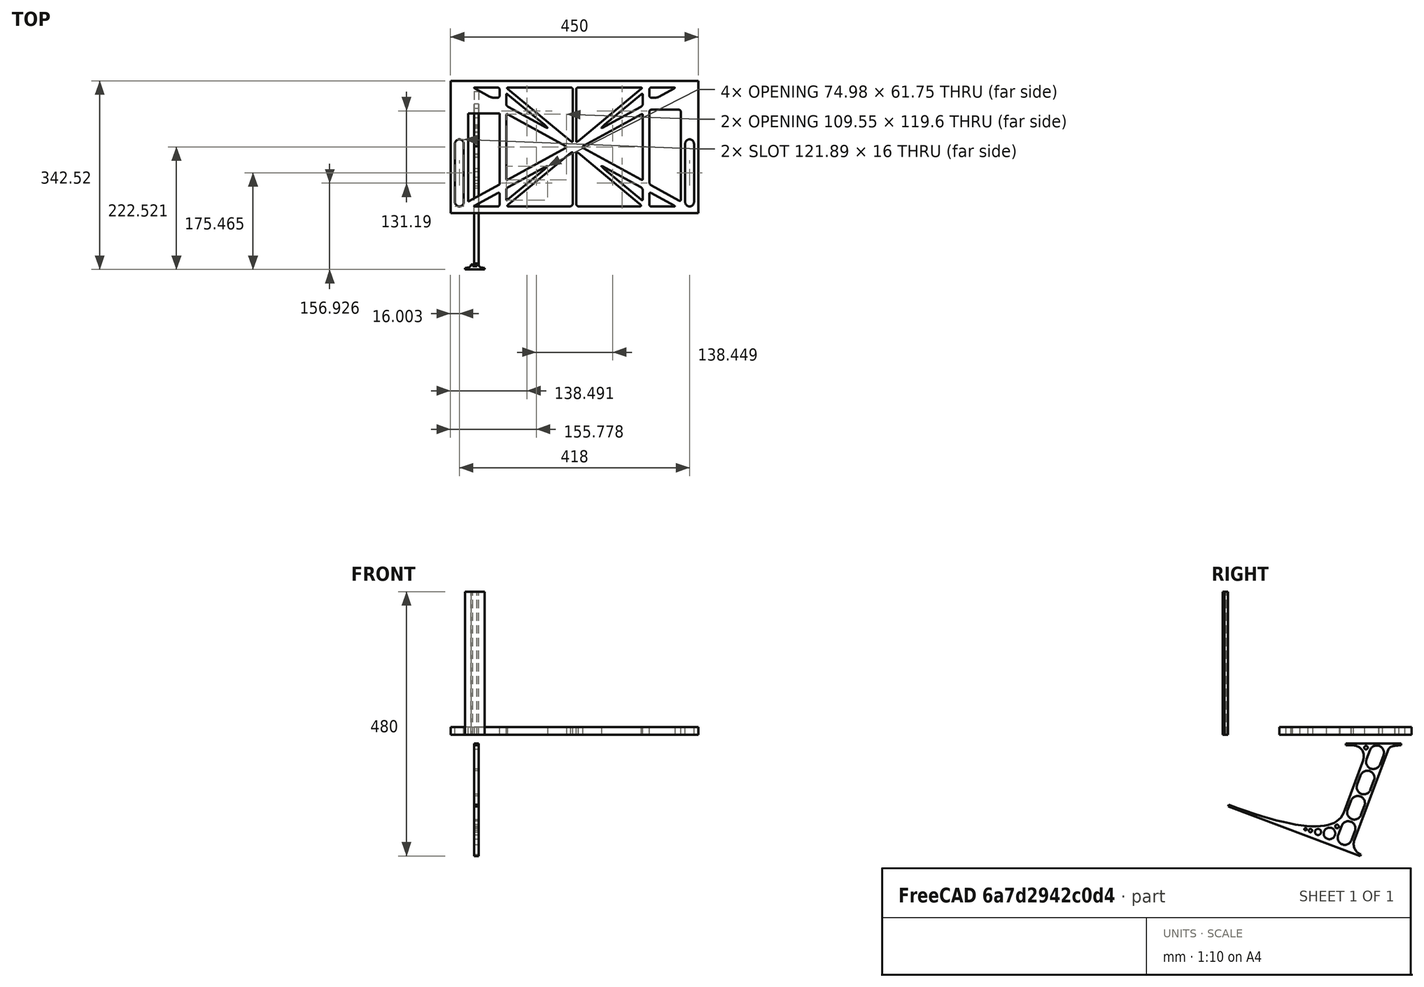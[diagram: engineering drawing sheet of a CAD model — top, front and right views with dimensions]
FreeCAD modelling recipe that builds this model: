
FCSTD DOCUMENT  (FreeCAD 0.19R0.19.2)
Label: laptopStand130FCStd
License: All rights reserved
LicenseURL: http://en.wikipedia.org/wiki/All_rights_reserved
objects: Sketcher::SketchObject×3, Part::Extrusion×3
note: 6 computed .brp shape members not serialized (recipe doc carries the construction recipe); baked Part::Feature solids carry a one-line shape summary decoded from their .brp

FEATURE [Sketcher::SketchObject] Sketch
  FullyConstrained = true
  sketch-geometry (351):
    g0: LineSegment StartX=-10.9272 StartY=-82.7794 StartZ=0 EndX=46.0728 EndY=-51.4823 EndZ=0
    g1: LineSegment StartX=-10.9272 StartY=76.4095 StartZ=0 EndX=-10.9272 EndY=-82.7794 EndZ=0
    g2: LineSegment StartX=46.0728 StartY=76.4095 StartZ=0 EndX=46.0728 EndY=-51.4823 EndZ=0
    g3: LineSegment StartX=-42.9272 StartY=136.221 StartZ=0 EndX=-42.9272 EndY=-103.779 EndZ=0
    g4: LineSegment StartX=407.073 StartY=136.221 StartZ=0 EndX=407.073 EndY=-103.779 EndZ=0
    g5: ArcOfCircle CenterX=-26.9272 CenterY=22.1087 CenterZ=0 NormalX=0 NormalY=0 NormalZ=1 AngleXU=0 Radius=8 StartAngle=1e-16 EndAngle=3.14159
    g6: ArcOfCircle CenterX=-26.9272 CenterY=-83.7794 CenterZ=0 NormalX=0 NormalY=0 NormalZ=1 AngleXU=0 Radius=8 StartAngle=3.14159 EndAngle=6.28319
    g7: LineSegment StartX=-34.9272 StartY=22.1087 StartZ=0 EndX=-34.9272 EndY=-83.7794 EndZ=0
    g8: LineSegment StartX=-18.9272 StartY=22.1087 StartZ=0 EndX=-18.9272 EndY=-83.7794 EndZ=0
    g9: ArcOfCircle CenterX=391.073 CenterY=22.1087 CenterZ=0 NormalX=0 NormalY=0 NormalZ=1 AngleXU=0 Radius=8 StartAngle=-4.4e-15 EndAngle=3.14159
    g10: LineSegment StartX=399.073 StartY=22.1087 StartZ=0 EndX=399.073 EndY=-83.7794 EndZ=0
    g11: LineSegment StartX=383.073 StartY=22.1087 StartZ=0 EndX=383.073 EndY=-83.7794 EndZ=0
    g12: ArcOfCircle CenterX=391.073 CenterY=-83.7794 CenterZ=0 NormalX=0 NormalY=0 NormalZ=1 AngleXU=0 Radius=8 StartAngle=3.14159 EndAngle=6.28319
    g13: Circle CenterX=175.022 CenterY=27.0628 CenterZ=0 NormalX=0 NormalY=0 NormalZ=1 AngleXU=0 Radius=1
    g14: Circle CenterX=179.022 CenterY=24.8665 CenterZ=0 NormalX=0 NormalY=0 NormalZ=1 AngleXU=0 Radius=1
    g15: Circle CenterX=179.022 CenterY=27.0628 CenterZ=0 NormalX=0 NormalY=0 NormalZ=1 AngleXU=0 Radius=1
    g16: BSplineCurve PolesCount=3 KnotsCount=2 Degree=2 IsPeriodic=0
    g17: GeomPoint X=175.022 Y=27.0628 Z=0
    g18: GeomPoint X=179.022 Y=27.0628 Z=0
    g19: Circle CenterX=189.124 CenterY=27.0628 CenterZ=0 NormalX=0 NormalY=0 NormalZ=1 AngleXU=0 Radius=1
    g20: Circle CenterX=185.124 CenterY=24.8665 CenterZ=0 NormalX=0 NormalY=0 NormalZ=1 AngleXU=0 Radius=1
    g21: Circle CenterX=185.124 CenterY=27.0628 CenterZ=0 NormalX=0 NormalY=0 NormalZ=1 AngleXU=0 Radius=1
    g22: BSplineCurve PolesCount=3 KnotsCount=2 Degree=2 IsPeriodic=0
    g23: GeomPoint X=189.124 Y=27.0628 Z=0
    g24: GeomPoint X=185.124 Y=27.0628 Z=0
    g25: Circle CenterX=175.022 CenterY=5.37834 CenterZ=0 NormalX=0 NormalY=0 NormalZ=1 AngleXU=0 Radius=1
    g26: Circle CenterX=179.022 CenterY=7.57463 CenterZ=0 NormalX=0 NormalY=0 NormalZ=1 AngleXU=0 Radius=1
    g27: Circle CenterX=179.022 CenterY=5.34704 CenterZ=0 NormalX=0 NormalY=0 NormalZ=1 AngleXU=0 Radius=1
    g28: BSplineCurve PolesCount=3 KnotsCount=2 Degree=2 IsPeriodic=0
    g29: GeomPoint X=175.022 Y=5.37834 Z=0
    g30: GeomPoint X=179.022 Y=5.34704 Z=0
    g31: Circle CenterX=189.124 CenterY=5.37834 CenterZ=0 NormalX=0 NormalY=0 NormalZ=1 AngleXU=0 Radius=1
    g32: Circle CenterX=185.124 CenterY=7.57463 CenterZ=0 NormalX=0 NormalY=0 NormalZ=1 AngleXU=0 Radius=1
    g33: Circle CenterX=185.124 CenterY=5.34704 CenterZ=0 NormalX=0 NormalY=0 NormalZ=1 AngleXU=0 Radius=1
    g34: BSplineCurve PolesCount=3 KnotsCount=2 Degree=2 IsPeriodic=0
    g35: GeomPoint X=189.124 Y=5.37834 Z=0
    g36: GeomPoint X=185.124 Y=5.34704 Z=0
    g37: Circle CenterX=165.871 CenterY=18.1458 CenterZ=0 NormalX=0 NormalY=0 NormalZ=1 AngleXU=0 Radius=1
    g38: Circle CenterX=169.377 CenterY=16.2206 CenterZ=0 NormalX=0 NormalY=0 NormalZ=1 AngleXU=0 Radius=1
    g39: Circle CenterX=165.871 CenterY=14.2954 CenterZ=0 NormalX=0 NormalY=0 NormalZ=1 AngleXU=0 Radius=1
    g40: BSplineCurve PolesCount=3 KnotsCount=2 Degree=2 IsPeriodic=0
    g41: GeomPoint X=165.871 Y=18.1458 Z=0
    g42: GeomPoint X=165.871 Y=14.2954 Z=0
    g43: Circle CenterX=198.275 CenterY=18.1458 CenterZ=0 NormalX=0 NormalY=0 NormalZ=1 AngleXU=0 Radius=1
    g44: Circle CenterX=194.768 CenterY=16.2206 CenterZ=0 NormalX=0 NormalY=0 NormalZ=1 AngleXU=0 Radius=1
    g45: Circle CenterX=198.275 CenterY=14.2954 CenterZ=0 NormalX=0 NormalY=0 NormalZ=1 AngleXU=0 Radius=1
    g46: BSplineCurve PolesCount=3 KnotsCount=2 Degree=2 IsPeriodic=0
    g47: GeomPoint X=198.275 Y=18.1458 Z=0
    g48: GeomPoint X=198.275 Y=14.2954 Z=0
    g49: LineSegment StartX=407.073 StartY=-103.779 StartZ=0 EndX=-42.9272 EndY=-103.779 EndZ=0
    g50: LineSegment StartX=407.073 StartY=136.221 StartZ=0 EndX=-42.9272 EndY=136.221 EndZ=0
    g51: LineSegment StartX=46.0728 StartY=76.4095 StartZ=0 EndX=-10.9272 EndY=76.4095 EndZ=0
    g52: Circle CenterX=125.607 CenterY=54.1951 CenterZ=0 NormalX=0 NormalY=0 NormalZ=1 AngleXU=0 Radius=1
    g53: Circle CenterX=139.632 CenterY=46.4944 CenterZ=0 NormalX=0 NormalY=0 NormalZ=1 AngleXU=0 Radius=1
    g54: Circle CenterX=127.326 CenterY=56.7187 CenterZ=0 NormalX=0 NormalY=0 NormalZ=1 AngleXU=0 Radius=1
    g55: BSplineCurve PolesCount=3 KnotsCount=2 Degree=2 IsPeriodic=0
    g56: GeomPoint X=125.607 Y=54.1951 Z=0
    g57: GeomPoint X=127.326 Y=56.7187 Z=0
    g58: Circle CenterX=236.821 CenterY=56.7187 CenterZ=0 NormalX=0 NormalY=0 NormalZ=1 AngleXU=0 Radius=1
    g59: Circle CenterX=224.513 CenterY=46.4944 CenterZ=0 NormalX=0 NormalY=0 NormalZ=1 AngleXU=0 Radius=1
    g60: Circle CenterX=238.538 CenterY=54.1951 CenterZ=0 NormalX=0 NormalY=0 NormalZ=1 AngleXU=0 Radius=1
    g61: BSplineCurve PolesCount=3 KnotsCount=2 Degree=2 IsPeriodic=0
    g62: GeomPoint X=236.821 Y=56.7187 Z=0
    g63: GeomPoint X=238.538 Y=54.1951 Z=0
    g64: Circle CenterX=238.538 CenterY=-21.7539 CenterZ=0 NormalX=0 NormalY=0 NormalZ=1 AngleXU=0 Radius=1
    g65: Circle CenterX=224.513 CenterY=-14.0532 CenterZ=0 NormalX=0 NormalY=0 NormalZ=1 AngleXU=0 Radius=1
    g66: Circle CenterX=236.821 CenterY=-24.2775 CenterZ=0 NormalX=0 NormalY=0 NormalZ=1 AngleXU=0 Radius=1
    g67: BSplineCurve PolesCount=3 KnotsCount=2 Degree=2 IsPeriodic=0
    g68: GeomPoint X=238.538 Y=-21.7539 Z=0
    g69: GeomPoint X=236.821 Y=-24.2775 Z=0
    g70: Circle CenterX=125.607 CenterY=-21.7539 CenterZ=0 NormalX=0 NormalY=0 NormalZ=1 AngleXU=0 Radius=1
    g71: Circle CenterX=139.632 CenterY=-14.0532 CenterZ=0 NormalX=0 NormalY=0 NormalZ=1 AngleXU=0 Radius=1
    g72: Circle CenterX=127.325 CenterY=-24.2775 CenterZ=0 NormalX=0 NormalY=0 NormalZ=1 AngleXU=0 Radius=1
    g73: BSplineCurve PolesCount=3 KnotsCount=2 Degree=2 IsPeriodic=0
    g74: GeomPoint X=125.607 Y=-21.7539 Z=0
    g75: GeomPoint X=127.325 Y=-24.2775 Z=0
    g76: Circle CenterX=302.996 CenterY=111.695 CenterZ=0 NormalX=0 NormalY=0 NormalZ=1 AngleXU=0 Radius=1
    g77: Circle CenterX=306.073 CenterY=114.251 CenterZ=0 NormalX=0 NormalY=0 NormalZ=1 AngleXU=0 Radius=1
    g78: Circle CenterX=306.073 CenterY=110.251 CenterZ=0 NormalX=0 NormalY=0 NormalZ=1 AngleXU=0 Radius=1
    g79: BSplineCurve PolesCount=3 KnotsCount=2 Degree=2 IsPeriodic=0
    g80: GeomPoint X=302.996 Y=111.695 Z=0
    g81: GeomPoint X=306.073 Y=110.251 Z=0
    g82: Circle CenterX=306.073 CenterY=95.2763 CenterZ=0 NormalX=0 NormalY=0 NormalZ=1 AngleXU=0 Radius=1
    g83: Circle CenterX=306.073 CenterY=91.2763 CenterZ=0 NormalX=0 NormalY=0 NormalZ=1 AngleXU=0 Radius=1
    g84: Circle CenterX=302.567 CenterY=89.3511 CenterZ=0 NormalX=0 NormalY=0 NormalZ=1 AngleXU=0 Radius=1
    g85: BSplineCurve PolesCount=3 KnotsCount=2 Degree=2 IsPeriodic=0
    g86: GeomPoint X=306.073 Y=95.2763 Z=0
    g87: GeomPoint X=302.567 Y=89.3511 Z=0
    g88: LineSegment StartX=306.073 StartY=110.251 StartZ=0 EndX=306.073 EndY=95.2763 EndZ=0
    g89: LineSegment StartX=302.996 StartY=111.695 StartZ=0 EndX=236.821 EndY=56.7187 EndZ=0
    g90: LineSegment StartX=238.538 StartY=54.1951 StartZ=0 EndX=302.567 EndY=89.3511 EndZ=0
    g91: Circle CenterX=61.1496 CenterY=111.695 CenterZ=0 NormalX=0 NormalY=0 NormalZ=1 AngleXU=0 Radius=1
    g92: Circle CenterX=58.0728 CenterY=114.251 CenterZ=0 NormalX=0 NormalY=0 NormalZ=1 AngleXU=0 Radius=1
    g93: Circle CenterX=58.0728 CenterY=110.251 CenterZ=0 NormalX=0 NormalY=0 NormalZ=1 AngleXU=0 Radius=1
    g94: BSplineCurve PolesCount=3 KnotsCount=2 Degree=2 IsPeriodic=0
    g95: GeomPoint X=61.1496 Y=111.695 Z=0
    g96: GeomPoint X=58.0728 Y=110.251 Z=0
    g97: Circle CenterX=61.5791 CenterY=89.3511 CenterZ=0 NormalX=0 NormalY=0 NormalZ=1 AngleXU=0 Radius=1
    g98: Circle CenterX=58.0728 CenterY=91.2763 CenterZ=0 NormalX=0 NormalY=0 NormalZ=1 AngleXU=0 Radius=1
    g99: Circle CenterX=58.0728 CenterY=95.2763 CenterZ=0 NormalX=0 NormalY=0 NormalZ=1 AngleXU=0 Radius=1
    g100: BSplineCurve PolesCount=3 KnotsCount=2 Degree=2 IsPeriodic=0
    g101: GeomPoint X=61.5791 Y=89.3511 Z=0
    g102: GeomPoint X=58.0728 Y=95.2763 Z=0
    g103: LineSegment StartX=58.0728 StartY=110.251 StartZ=0 EndX=58.0728 EndY=95.2763 EndZ=0
    g104: LineSegment StartX=61.1496 StartY=111.695 StartZ=0 EndX=127.326 EndY=56.7187 EndZ=0
    g105: LineSegment StartX=125.607 StartY=54.1951 StartZ=0 EndX=61.5791 EndY=89.3511 EndZ=0
    g106: Circle CenterX=61.5791 CenterY=-56.9099 CenterZ=0 NormalX=0 NormalY=0 NormalZ=1 AngleXU=0 Radius=1
    g107: Circle CenterX=58.0728 CenterY=-58.8351 CenterZ=0 NormalX=0 NormalY=0 NormalZ=1 AngleXU=0 Radius=1
    g108: Circle CenterX=58.0728 CenterY=-62.8351 CenterZ=0 NormalX=0 NormalY=0 NormalZ=1 AngleXU=0 Radius=1
    g109: BSplineCurve PolesCount=3 KnotsCount=2 Degree=2 IsPeriodic=0
    g110: GeomPoint X=61.5791 Y=-56.9099 Z=0
    g111: GeomPoint X=58.0728 Y=-62.8351 Z=0
    g112: Circle CenterX=58.0728 CenterY=-77.8102 CenterZ=0 NormalX=0 NormalY=0 NormalZ=1 AngleXU=0 Radius=1
    g113: Circle CenterX=58.0728 CenterY=-81.8102 CenterZ=0 NormalX=0 NormalY=0 NormalZ=1 AngleXU=0 Radius=1
    g114: Circle CenterX=61.1496 CenterY=-79.2541 CenterZ=0 NormalX=0 NormalY=0 NormalZ=1 AngleXU=0 Radius=1
    g115: BSplineCurve PolesCount=3 KnotsCount=2 Degree=2 IsPeriodic=0
    g116: GeomPoint X=58.0728 Y=-77.8102 Z=0
    g117: GeomPoint X=61.1496 Y=-79.2541 Z=0
    g118: LineSegment StartX=58.0728 StartY=-62.8351 StartZ=0 EndX=58.0728 EndY=-77.8102 EndZ=0
    g119: LineSegment StartX=61.1496 StartY=-79.2541 StartZ=0 EndX=127.325 EndY=-24.2775 EndZ=0
    g120: LineSegment StartX=125.607 StartY=-21.7539 StartZ=0 EndX=61.5791 EndY=-56.9099 EndZ=0
    g121: Circle CenterX=302.567 CenterY=-56.9099 CenterZ=0 NormalX=0 NormalY=0 NormalZ=1 AngleXU=0 Radius=1
    g122: Circle CenterX=306.073 CenterY=-58.8351 CenterZ=0 NormalX=0 NormalY=0 NormalZ=1 AngleXU=0 Radius=1
    g123: Circle CenterX=306.073 CenterY=-62.8351 CenterZ=0 NormalX=0 NormalY=0 NormalZ=1 AngleXU=0 Radius=1
    g124: BSplineCurve PolesCount=3 KnotsCount=2 Degree=2 IsPeriodic=0
    g125: GeomPoint X=302.567 Y=-56.9099 Z=0
    g126: GeomPoint X=306.073 Y=-62.8351 Z=0
    g127: Circle CenterX=302.996 CenterY=-79.2541 CenterZ=0 NormalX=0 NormalY=0 NormalZ=1 AngleXU=0 Radius=1
    g128: Circle CenterX=306.073 CenterY=-81.8102 CenterZ=0 NormalX=0 NormalY=0 NormalZ=1 AngleXU=0 Radius=1
    g129: Circle CenterX=306.073 CenterY=-77.8102 CenterZ=0 NormalX=0 NormalY=0 NormalZ=1 AngleXU=0 Radius=1
    g130: BSplineCurve PolesCount=3 KnotsCount=2 Degree=2 IsPeriodic=0
    g131: GeomPoint X=302.996 Y=-79.2541 Z=0
    g132: GeomPoint X=306.073 Y=-77.8102 Z=0
    g133: LineSegment StartX=306.073 StartY=-62.8351 StartZ=0 EndX=306.073 EndY=-77.8102 EndZ=0
    g134: LineSegment StartX=302.996 StartY=-79.2541 StartZ=0 EndX=236.821 EndY=-24.2775 EndZ=0
    g135: LineSegment StartX=238.538 StartY=-21.7539 StartZ=0 EndX=302.567 EndY=-56.9099 EndZ=0
    g136: Circle CenterX=61.6457 CenterY=-88.8112 CenterZ=0 NormalX=0 NormalY=0 NormalZ=1 AngleXU=0 Radius=1
    g137: Circle CenterX=58.0728 CenterY=-91.7794 CenterZ=0 NormalX=0 NormalY=0 NormalZ=1 AngleXU=0 Radius=1
    g138: Circle CenterX=63.9135 CenterY=-91.7794 CenterZ=0 NormalX=0 NormalY=0 NormalZ=1 AngleXU=0 Radius=1
    g139: BSplineCurve PolesCount=3 KnotsCount=2 Degree=2 IsPeriodic=0
    g140: GeomPoint X=61.6457 Y=-88.8112 Z=0
    g141: GeomPoint X=63.9135 Y=-91.7794 Z=0
    g142: Circle CenterX=179.022 CenterY=-85.8163 CenterZ=0 NormalX=0 NormalY=0 NormalZ=1 AngleXU=0 Radius=1
    g143: Circle CenterX=179.022 CenterY=-91.7794 CenterZ=0 NormalX=0 NormalY=0 NormalZ=1 AngleXU=0 Radius=1
    g144: Circle CenterX=171.895 CenterY=-91.7794 CenterZ=0 NormalX=0 NormalY=0 NormalZ=1 AngleXU=0 Radius=1
    g145: BSplineCurve PolesCount=3 KnotsCount=2 Degree=2 IsPeriodic=0
    g146: GeomPoint X=179.022 Y=-85.8163 Z=0
    g147: GeomPoint X=171.895 Y=-91.7794 Z=0
    g148: Circle CenterX=185.124 CenterY=-86.2028 CenterZ=0 NormalX=0 NormalY=0 NormalZ=1 AngleXU=0 Radius=1
    g149: Circle CenterX=185.124 CenterY=-91.7794 CenterZ=0 NormalX=0 NormalY=0 NormalZ=1 AngleXU=0 Radius=1
    g150: Circle CenterX=191.747 CenterY=-91.7794 CenterZ=0 NormalX=0 NormalY=0 NormalZ=1 AngleXU=0 Radius=1
    g151: BSplineCurve PolesCount=3 KnotsCount=2 Degree=2 IsPeriodic=0
    g152: GeomPoint X=185.124 Y=-86.2028 Z=0
    g153: GeomPoint X=191.747 Y=-91.7794 Z=0
    g154: Circle CenterX=299.888 CenterY=-86.6413 CenterZ=0 NormalX=0 NormalY=0 NormalZ=1 AngleXU=0 Radius=1
    g155: Circle CenterX=306.073 CenterY=-91.7794 CenterZ=0 NormalX=0 NormalY=0 NormalZ=1 AngleXU=0 Radius=1
    g156: Circle CenterX=298.776 CenterY=-91.7794 CenterZ=0 NormalX=0 NormalY=0 NormalZ=1 AngleXU=0 Radius=1
    g157: BSplineCurve PolesCount=3 KnotsCount=2 Degree=2 IsPeriodic=0
    g158: GeomPoint X=299.888 Y=-86.6413 Z=0
    g159: GeomPoint X=298.776 Y=-91.7794 Z=0
    g160: LineSegment StartX=189.124 StartY=5.37834 StartZ=0 EndX=299.888 EndY=-86.6413 EndZ=0
    g161: LineSegment StartX=298.776 StartY=-91.7794 StartZ=0 EndX=191.747 EndY=-91.7794 EndZ=0
    g162: LineSegment StartX=185.124 StartY=-86.2028 StartZ=0 EndX=185.124 EndY=5.34704 EndZ=0
    g163: LineSegment StartX=179.022 StartY=5.34704 StartZ=0 EndX=179.022 EndY=-85.8163 EndZ=0
    g164: LineSegment StartX=171.895 StartY=-91.7794 StartZ=0 EndX=63.9135 EndY=-91.7794 EndZ=0
    g165: LineSegment StartX=61.6457 StartY=-88.8112 StartZ=0 EndX=175.022 EndY=5.37834 EndZ=0
    g166: Circle CenterX=302.073 CenterY=124.221 CenterZ=0 NormalX=0 NormalY=0 NormalZ=1 AngleXU=0 Radius=1
    g167: Circle CenterX=306.073 CenterY=124.221 CenterZ=0 NormalX=0 NormalY=0 NormalZ=1 AngleXU=0 Radius=1
    g168: Circle CenterX=302.996 CenterY=121.665 CenterZ=0 NormalX=0 NormalY=0 NormalZ=1 AngleXU=0 Radius=1
    g169: BSplineCurve PolesCount=3 KnotsCount=2 Degree=2 IsPeriodic=0
    g170: GeomPoint X=302.073 Y=124.221 Z=0
    g171: GeomPoint X=302.996 Y=121.665 Z=0
    g172: Circle CenterX=189.124 CenterY=124.221 CenterZ=0 NormalX=0 NormalY=0 NormalZ=1 AngleXU=0 Radius=1
    g173: Circle CenterX=185.124 CenterY=124.221 CenterZ=0 NormalX=0 NormalY=0 NormalZ=1 AngleXU=0 Radius=1
    g174: Circle CenterX=185.124 CenterY=120.221 CenterZ=0 NormalX=0 NormalY=0 NormalZ=1 AngleXU=0 Radius=1
    g175: BSplineCurve PolesCount=3 KnotsCount=2 Degree=2 IsPeriodic=0
    g176: GeomPoint X=189.124 Y=124.221 Z=0
    g177: GeomPoint X=185.124 Y=120.221 Z=0
    g178: Circle CenterX=175.022 CenterY=124.221 CenterZ=0 NormalX=0 NormalY=0 NormalZ=1 AngleXU=0 Radius=1
    g179: Circle CenterX=179.022 CenterY=124.221 CenterZ=0 NormalX=0 NormalY=0 NormalZ=1 AngleXU=0 Radius=1
    g180: Circle CenterX=179.022 CenterY=120.221 CenterZ=0 NormalX=0 NormalY=0 NormalZ=1 AngleXU=0 Radius=1
    g181: BSplineCurve PolesCount=3 KnotsCount=2 Degree=2 IsPeriodic=0
    g182: GeomPoint X=175.022 Y=124.221 Z=0
    g183: GeomPoint X=179.022 Y=120.221 Z=0
    g184: Circle CenterX=62.0728 CenterY=124.221 CenterZ=0 NormalX=0 NormalY=0 NormalZ=1 AngleXU=0 Radius=1
    g185: Circle CenterX=58.0728 CenterY=124.221 CenterZ=0 NormalX=0 NormalY=0 NormalZ=1 AngleXU=0 Radius=1
    g186: Circle CenterX=61.1496 CenterY=121.665 CenterZ=0 NormalX=0 NormalY=0 NormalZ=1 AngleXU=0 Radius=1
    g187: BSplineCurve PolesCount=3 KnotsCount=2 Degree=2 IsPeriodic=0
    g188: GeomPoint X=62.0728 Y=124.221 Z=0
    g189: GeomPoint X=61.1496 Y=121.665 Z=0
    g190: LineSegment StartX=62.0728 StartY=124.221 StartZ=0 EndX=175.022 EndY=124.221 EndZ=0
    g191: LineSegment StartX=179.022 StartY=120.221 StartZ=0 EndX=179.022 EndY=27.0628 EndZ=0
    g192: LineSegment StartX=185.124 StartY=27.0628 StartZ=0 EndX=185.124 EndY=120.221 EndZ=0
    g193: LineSegment StartX=189.124 StartY=124.221 StartZ=0 EndX=302.073 EndY=124.221 EndZ=0
    g194: LineSegment StartX=302.996 StartY=121.665 StartZ=0 EndX=189.124 EndY=27.0628 EndZ=0
    g195: LineSegment StartX=175.022 StartY=27.0628 StartZ=0 EndX=61.1496 EndY=121.665 EndZ=0
    g196: Circle CenterX=61.5791 CenterY=75.4095 CenterZ=0 NormalX=0 NormalY=0 NormalZ=1 AngleXU=0 Radius=1
    g197: Circle CenterX=58.0728 CenterY=77.3346 CenterZ=0 NormalX=0 NormalY=0 NormalZ=1 AngleXU=0 Radius=1
    g198: Circle CenterX=58.0728 CenterY=73.3346 CenterZ=0 NormalX=0 NormalY=0 NormalZ=1 AngleXU=0 Radius=1
    g199: BSplineCurve PolesCount=3 KnotsCount=2 Degree=2 IsPeriodic=0
    g200: GeomPoint X=61.5791 Y=75.4095 Z=0
    g201: GeomPoint X=58.0728 Y=73.3346 Z=0
    g202: Circle CenterX=58.0728 CenterY=-40.8935 CenterZ=0 NormalX=0 NormalY=0 NormalZ=1 AngleXU=0 Radius=1
    g203: Circle CenterX=58.0728 CenterY=-44.8935 CenterZ=0 NormalX=0 NormalY=0 NormalZ=1 AngleXU=0 Radius=1
    g204: Circle CenterX=61.5791 CenterY=-42.9683 CenterZ=0 NormalX=0 NormalY=0 NormalZ=1 AngleXU=0 Radius=1
    g205: BSplineCurve PolesCount=3 KnotsCount=2 Degree=2 IsPeriodic=0
    g206: GeomPoint X=58.0728 Y=-40.8935 Z=0
    g207: GeomPoint X=61.5791 Y=-42.9683 Z=0
    g208: LineSegment StartX=61.5791 StartY=-42.9683 StartZ=0 EndX=165.871 EndY=14.2954 EndZ=0
    g209: LineSegment StartX=165.871 StartY=18.1458 StartZ=0 EndX=61.5791 EndY=75.4095 EndZ=0
    g210: LineSegment StartX=58.0728 StartY=73.3346 StartZ=0 EndX=58.0728 EndY=-40.8935 EndZ=0
    g211: Circle CenterX=302.567 CenterY=-42.9683 CenterZ=0 NormalX=0 NormalY=0 NormalZ=1 AngleXU=0 Radius=1
    g212: Circle CenterX=306.073 CenterY=-44.8935 CenterZ=0 NormalX=0 NormalY=0 NormalZ=1 AngleXU=0 Radius=1
    g213: Circle CenterX=306.073 CenterY=-40.8935 CenterZ=0 NormalX=0 NormalY=0 NormalZ=1 AngleXU=0 Radius=1
    g214: BSplineCurve PolesCount=3 KnotsCount=2 Degree=2 IsPeriodic=0
    g215: GeomPoint X=302.567 Y=-42.9683 Z=0
    g216: GeomPoint X=306.073 Y=-40.8935 Z=0
    g217: Circle CenterX=306.073 CenterY=73.3346 CenterZ=0 NormalX=0 NormalY=0 NormalZ=1 AngleXU=0 Radius=1
    g218: Circle CenterX=306.073 CenterY=77.3346 CenterZ=0 NormalX=0 NormalY=0 NormalZ=1 AngleXU=0 Radius=1
    g219: Circle CenterX=302.567 CenterY=75.4095 CenterZ=0 NormalX=0 NormalY=0 NormalZ=1 AngleXU=0 Radius=1
    g220: BSplineCurve PolesCount=3 KnotsCount=2 Degree=2 IsPeriodic=0
    g221: GeomPoint X=306.073 Y=73.3346 Z=0
    g222: GeomPoint X=302.567 Y=75.4095 Z=0
    g223: LineSegment StartX=302.567 StartY=-42.9683 StartZ=0 EndX=198.275 EndY=14.2954 EndZ=0
    g224: LineSegment StartX=198.275 StartY=18.1458 StartZ=0 EndX=302.567 EndY=75.4095 EndZ=0
    g225: LineSegment StartX=306.073 StartY=73.3346 StartZ=0 EndX=306.073 EndY=-40.8935 EndZ=0
    g226: LineSegment StartX=322.073 StartY=105.865 StartZ=0 EndX=328.643 EndY=105.865 EndZ=0
    g227: LineSegment StartX=318.073 StartY=120.221 StartZ=0 EndX=318.073 EndY=109.865 EndZ=0
    g228: LineSegment StartX=336.157 StartY=107.779 StartZ=0 EndX=362.567 EndY=122.294 EndZ=0
    g229: Circle CenterX=362.073 CenterY=124.221 CenterZ=0 NormalX=0 NormalY=0 NormalZ=1 AngleXU=0 Radius=1
    g230: Circle CenterX=366.073 CenterY=124.221 CenterZ=0 NormalX=0 NormalY=0 NormalZ=1 AngleXU=0 Radius=1
    g231: Circle CenterX=362.567 CenterY=122.294 CenterZ=0 NormalX=0 NormalY=0 NormalZ=1 AngleXU=0 Radius=1
    g232: BSplineCurve PolesCount=3 KnotsCount=2 Degree=2 IsPeriodic=0
    g233: GeomPoint X=362.073 Y=124.221 Z=0
    g234: GeomPoint X=362.567 Y=122.294 Z=0
    g235: Circle CenterX=322.073 CenterY=124.221 CenterZ=0 NormalX=0 NormalY=0 NormalZ=1 AngleXU=0 Radius=1
    g236: Circle CenterX=318.073 CenterY=124.221 CenterZ=0 NormalX=0 NormalY=0 NormalZ=1 AngleXU=0 Radius=1
    g237: Circle CenterX=318.073 CenterY=120.221 CenterZ=0 NormalX=0 NormalY=0 NormalZ=1 AngleXU=0 Radius=1
    g238: BSplineCurve PolesCount=3 KnotsCount=2 Degree=2 IsPeriodic=0
    g239: GeomPoint X=322.073 Y=124.221 Z=0
    g240: GeomPoint X=318.073 Y=120.221 Z=0
    g241: Circle CenterX=322.073 CenterY=105.865 CenterZ=0 NormalX=0 NormalY=0 NormalZ=1 AngleXU=0 Radius=1
    g242: Circle CenterX=318.073 CenterY=105.865 CenterZ=0 NormalX=0 NormalY=0 NormalZ=1 AngleXU=0 Radius=1
    g243: Circle CenterX=318.073 CenterY=109.865 CenterZ=0 NormalX=0 NormalY=0 NormalZ=1 AngleXU=0 Radius=1
    g244: BSplineCurve PolesCount=3 KnotsCount=2 Degree=2 IsPeriodic=0
    g245: GeomPoint X=322.073 Y=105.865 Z=0
    g246: GeomPoint X=318.073 Y=109.865 Z=0
    g247: Circle CenterX=336.157 CenterY=107.779 CenterZ=0 NormalX=0 NormalY=0 NormalZ=1 AngleXU=0 Radius=1
    g248: Circle CenterX=332.651 CenterY=105.853 CenterZ=0 NormalX=0 NormalY=0 NormalZ=1 AngleXU=0 Radius=1
    g249: Circle CenterX=328.643 CenterY=105.865 CenterZ=0 NormalX=0 NormalY=0 NormalZ=1 AngleXU=0 Radius=1
    g250: BSplineCurve PolesCount=3 KnotsCount=2 Degree=2 IsPeriodic=0
    g251: GeomPoint X=336.157 Y=107.779 Z=0
    g252: GeomPoint X=328.643 Y=105.865 Z=0
    g253: LineSegment StartX=322.073 StartY=124.221 StartZ=0 EndX=362.073 EndY=124.221 EndZ=0
    g254: Circle CenterX=371.567 CenterY=-80.8644 CenterZ=0 NormalX=0 NormalY=0 NormalZ=1 AngleXU=0 Radius=1
    g255: Circle CenterX=375.073 CenterY=-82.7896 CenterZ=0 NormalX=0 NormalY=0 NormalZ=1 AngleXU=0 Radius=1
    g256: Circle CenterX=375.073 CenterY=-78.7896 CenterZ=0 NormalX=0 NormalY=0 NormalZ=1 AngleXU=0 Radius=1
    g257: BSplineCurve PolesCount=3 KnotsCount=2 Degree=2 IsPeriodic=0
    g258: GeomPoint X=371.567 Y=-80.8644 Z=0
    g259: GeomPoint X=375.073 Y=-78.7896 Z=0
    g260: Circle CenterX=321.579 CenterY=-53.4075 CenterZ=0 NormalX=0 NormalY=0 NormalZ=1 AngleXU=0 Radius=1
    g261: Circle CenterX=318.073 CenterY=-51.4823 CenterZ=0 NormalX=0 NormalY=0 NormalZ=1 AngleXU=0 Radius=1
    g262: Circle CenterX=318.073 CenterY=-47.4823 CenterZ=0 NormalX=0 NormalY=0 NormalZ=1 AngleXU=0 Radius=1
    g263: BSplineCurve PolesCount=3 KnotsCount=2 Degree=2 IsPeriodic=0
    g264: GeomPoint X=321.579 Y=-53.4075 Z=0
    g265: GeomPoint X=318.073 Y=-47.4823 Z=0
    g266: Circle CenterX=375.073 CenterY=79.9235 CenterZ=0 NormalX=0 NormalY=0 NormalZ=1 AngleXU=0 Radius=1
    g267: Circle CenterX=375.073 CenterY=83.9235 CenterZ=0 NormalX=0 NormalY=0 NormalZ=1 AngleXU=0 Radius=1
    g268: Circle CenterX=371.073 CenterY=83.9235 CenterZ=0 NormalX=0 NormalY=0 NormalZ=1 AngleXU=0 Radius=1
    g269: BSplineCurve PolesCount=3 KnotsCount=2 Degree=2 IsPeriodic=0
    g270: GeomPoint X=375.073 Y=79.9235 Z=0
    g271: GeomPoint X=371.073 Y=83.9235 Z=0
    g272: LineSegment StartX=375.073 StartY=79.9235 StartZ=0 EndX=375.073 EndY=78.9235 EndZ=0
    g273: LineSegment StartX=371.567 StartY=-80.8644 StartZ=0 EndX=321.579 EndY=-53.4075 EndZ=0
    g274: LineSegment StartX=318.073 StartY=-47.4823 StartZ=0 EndX=318.073 EndY=76.4095 EndZ=0
    g275: Circle CenterX=321.579 CenterY=-67.3492 CenterZ=0 NormalX=0 NormalY=0 NormalZ=1 AngleXU=0 Radius=1
    g276: Circle CenterX=318.073 CenterY=-65.424 CenterZ=0 NormalX=0 NormalY=0 NormalZ=1 AngleXU=0 Radius=1
    g277: Circle CenterX=318.073 CenterY=-69.424 CenterZ=0 NormalX=0 NormalY=0 NormalZ=1 AngleXU=0 Radius=1
    g278: BSplineCurve PolesCount=3 KnotsCount=2 Degree=2 IsPeriodic=0
    g279: GeomPoint X=321.579 Y=-67.3492 Z=0
    g280: GeomPoint X=318.073 Y=-69.424 Z=0
    g281: Circle CenterX=362.567 CenterY=-89.8542 CenterZ=0 NormalX=0 NormalY=0 NormalZ=1 AngleXU=0 Radius=1
    g282: Circle CenterX=366.073 CenterY=-91.7794 CenterZ=0 NormalX=0 NormalY=0 NormalZ=1 AngleXU=0 Radius=1
    g283: Circle CenterX=362.073 CenterY=-91.7794 CenterZ=0 NormalX=0 NormalY=0 NormalZ=1 AngleXU=0 Radius=1
    g284: BSplineCurve PolesCount=3 KnotsCount=2 Degree=2 IsPeriodic=0
    g285: GeomPoint X=362.567 Y=-89.8542 Z=0
    g286: GeomPoint X=362.073 Y=-91.7794 Z=0
    g287: Circle CenterX=322.073 CenterY=-91.7794 CenterZ=0 NormalX=0 NormalY=0 NormalZ=1 AngleXU=0 Radius=1
    g288: Circle CenterX=318.073 CenterY=-91.7794 CenterZ=0 NormalX=0 NormalY=0 NormalZ=1 AngleXU=0 Radius=1
    g289: Circle CenterX=318.073 CenterY=-87.7794 CenterZ=0 NormalX=0 NormalY=0 NormalZ=1 AngleXU=0 Radius=1
    g290: BSplineCurve PolesCount=3 KnotsCount=2 Degree=2 IsPeriodic=0
    g291: GeomPoint X=322.073 Y=-91.7794 Z=0
    g292: GeomPoint X=318.073 Y=-87.7794 Z=0
    g293: LineSegment StartX=362.567 StartY=-89.8542 StartZ=0 EndX=321.579 EndY=-67.3492 EndZ=0
    g294: LineSegment StartX=318.073 StartY=-69.424 StartZ=0 EndX=318.073 EndY=-87.7794 EndZ=0
    g295: LineSegment StartX=322.073 StartY=-91.7794 StartZ=0 EndX=362.073 EndY=-91.7794 EndZ=0
    g296: Circle CenterX=2.07281 CenterY=124.221 CenterZ=0 NormalX=0 NormalY=0 NormalZ=1 AngleXU=0 Radius=1
    g297: Circle CenterX=1.57905 CenterY=122.295 CenterZ=0 NormalX=0 NormalY=0 NormalZ=1 AngleXU=0 Radius=1
    g298: BSplineCurve PolesCount=3 KnotsCount=2 Degree=2 IsPeriodic=0
    g299: GeomPoint X=2.07281 Y=124.221 Z=0
    g300: GeomPoint X=1.57905 Y=122.295 Z=0
    g301: Circle CenterX=42.0728 CenterY=124.221 CenterZ=0 NormalX=0 NormalY=0 NormalZ=1 AngleXU=0 Radius=1
    g302: Circle CenterX=46.0728 CenterY=124.221 CenterZ=0 NormalX=0 NormalY=0 NormalZ=1 AngleXU=0 Radius=1
    g303: Circle CenterX=46.0728 CenterY=120.221 CenterZ=0 NormalX=0 NormalY=0 NormalZ=1 AngleXU=0 Radius=1
    g304: BSplineCurve PolesCount=3 KnotsCount=2 Degree=2 IsPeriodic=0
    g305: GeomPoint X=42.0728 Y=124.221 Z=0
    g306: GeomPoint X=46.0728 Y=120.221 Z=0
    g307: Circle CenterX=46.0728 CenterY=109.865 CenterZ=0 NormalX=0 NormalY=0 NormalZ=1 AngleXU=0 Radius=1
    g308: Circle CenterX=46.0728 CenterY=105.865 CenterZ=0 NormalX=0 NormalY=0 NormalZ=1 AngleXU=0 Radius=1
    g309: Circle CenterX=42.0728 CenterY=105.865 CenterZ=0 NormalX=0 NormalY=0 NormalZ=1 AngleXU=0 Radius=1
    g310: BSplineCurve PolesCount=3 KnotsCount=2 Degree=2 IsPeriodic=0
    g311: GeomPoint X=46.0728 Y=109.865 Z=0
    g312: GeomPoint X=42.0728 Y=105.865 Z=0
    g313: Circle CenterX=35.5028 CenterY=105.865 CenterZ=0 NormalX=0 NormalY=0 NormalZ=1 AngleXU=0 Radius=1
    g314: Circle CenterX=31.5028 CenterY=105.865 CenterZ=0 NormalX=0 NormalY=0 NormalZ=1 AngleXU=0 Radius=1
    g315: Circle CenterX=27.9965 CenterY=107.79 CenterZ=0 NormalX=0 NormalY=0 NormalZ=1 AngleXU=0 Radius=1
    g316: BSplineCurve PolesCount=3 KnotsCount=2 Degree=2 IsPeriodic=0
    g317: GeomPoint X=35.5028 Y=105.865 Z=0
    g318: GeomPoint X=27.9965 Y=107.79 Z=0
    g319: LineSegment StartX=2.07281 StartY=124.221 StartZ=0 EndX=42.0728 EndY=124.221 EndZ=0
    g320: LineSegment StartX=46.0728 StartY=120.221 StartZ=0 EndX=46.0728 EndY=109.865 EndZ=0
    g321: LineSegment StartX=42.0728 StartY=105.865 StartZ=0 EndX=35.5028 EndY=105.865 EndZ=0
    g322: LineSegment StartX=27.9965 StartY=107.79 StartZ=0 EndX=1.57905 EndY=122.295 EndZ=0
    g323: Circle CenterX=42.5666 CenterY=-67.3492 CenterZ=0 NormalX=0 NormalY=0 NormalZ=1 AngleXU=0 Radius=1
    g324: Circle CenterX=46.0728 CenterY=-65.424 CenterZ=0 NormalX=0 NormalY=0 NormalZ=1 AngleXU=0 Radius=1
    g325: Circle CenterX=46.0728 CenterY=-69.424 CenterZ=0 NormalX=0 NormalY=0 NormalZ=1 AngleXU=0 Radius=1
    g326: BSplineCurve PolesCount=3 KnotsCount=2 Degree=2 IsPeriodic=0
    g327: GeomPoint X=42.5666 Y=-67.3492 Z=0
    g328: GeomPoint X=46.0728 Y=-69.424 Z=0
    g329: Circle CenterX=46.0728 CenterY=-87.7794 CenterZ=0 NormalX=0 NormalY=0 NormalZ=1 AngleXU=0 Radius=1
    g330: Circle CenterX=46.0728 CenterY=-91.7794 CenterZ=0 NormalX=0 NormalY=0 NormalZ=1 AngleXU=0 Radius=1
    g331: Circle CenterX=42.0728 CenterY=-91.7794 CenterZ=0 NormalX=0 NormalY=0 NormalZ=1 AngleXU=0 Radius=1
    g332: BSplineCurve PolesCount=3 KnotsCount=2 Degree=2 IsPeriodic=0
    g333: GeomPoint X=46.0728 Y=-87.7794 Z=0
    g334: GeomPoint X=42.0728 Y=-91.7794 Z=0
    g335: Circle CenterX=2.07281 CenterY=-91.7794 CenterZ=0 NormalX=0 NormalY=0 NormalZ=1 AngleXU=0 Radius=1
    g336: Circle CenterX=-1.92719 CenterY=-91.7794 CenterZ=0 NormalX=0 NormalY=0 NormalZ=1 AngleXU=0 Radius=1
    g337: Circle CenterX=1.57905 CenterY=-89.8542 CenterZ=0 NormalX=0 NormalY=0 NormalZ=1 AngleXU=0 Radius=1
    g338: BSplineCurve PolesCount=3 KnotsCount=2 Degree=2 IsPeriodic=0
    g339: GeomPoint X=2.07281 Y=-91.7794 Z=0
    g340: GeomPoint X=1.57905 Y=-89.8542 Z=0
    g341: LineSegment StartX=2.07281 StartY=-91.7794 StartZ=0 EndX=42.0728 EndY=-91.7794 EndZ=0
    g342: LineSegment StartX=46.0728 StartY=-87.7794 StartZ=0 EndX=46.0728 EndY=-69.424 EndZ=0
    g343: LineSegment StartX=42.5666 StartY=-67.3492 StartZ=0 EndX=1.57905 EndY=-89.8542 EndZ=0
    g344: LineSegment StartX=318.073 StartY=76.4095 StartZ=0 EndX=375.073 EndY=76.4095 EndZ=0
    g345: LineSegment StartX=375.073 StartY=76.4095 StartZ=0 EndX=375.073 EndY=-78.7896 EndZ=0
    g346: LineSegment StartX=318.073 StartY=76.4095 StartZ=0 EndX=322.073 EndY=76.4095 EndZ=0
    g347: Circle CenterX=322.073 CenterY=76.4095 CenterZ=0 NormalX=0 NormalY=0 NormalZ=1 AngleXU=0 Radius=1
    g348: BSplineCurve PolesCount=3 KnotsCount=2 Degree=2 IsPeriodic=0
    g349: GeomPoint X=318.073 Y=72.4095 Z=0
    g350: GeomPoint X=322.073 Y=76.4095 Z=0
  constraints (582):
    c: Coincident(g0,g2)
    c: Block(g0)
    c: Block(g1)
    c: Vertical(g3)
    c: Vertical(g4)
    c: Block(g4)
    c: Block(g3)
    c: Tangent(g5,g8) = 1.5708
    c: Tangent(g5,g7) = -1.5708
    c: Tangent(g7,g6) = -1.5708
    c: Tangent(g8,g6) = 1.5708
    c: Vertical(g7)
    c: Equal(g5,g6)
    c: Block(g8)
    c: Block(g7)
    c: Tangent(g9,g10) = 1.5708
    c: Tangent(g10,g12) = 1.5708
    c: Equal(g9,g12)
    c: Coincident(g11,g9)
    c: Coincident(g11,g12)
    c: Block(g10)
    c: Block(g11)
    c: Weight(g13) = 1
    c: Equal(g13,g14)
    c: Equal(g13,g15)
    c: InternalAlignment(g13,g16)
    c: InternalAlignment(g14,g16)
    c: InternalAlignment(g15,g16)
    c: InternalAlignment(g17,g16)
    c: InternalAlignment(g18,g16)
    c: Weight(g19) = 1
    c: Equal(g19,g20)
    c: Equal(g19,g21)
    c: InternalAlignment(g19,g22)
    c: InternalAlignment(g20,g22)
    c: InternalAlignment(g21,g22)
    c: InternalAlignment(g23,g22)
    c: InternalAlignment(g24,g22)
    c: Block(g22)
    c: Block(g16)
    c: Weight(g25) = 1
    c: Equal(g25,g26)
    c: Equal(g25,g27)
    c: InternalAlignment(g25,g28)
    c: InternalAlignment(g26,g28)
    c: InternalAlignment(g27,g28)
    c: InternalAlignment(g29,g28)
    c: InternalAlignment(g30,g28)
    c: Weight(g31) = 1
    c: Equal(g31,g32)
    c: Equal(g31,g33)
    c: InternalAlignment(g31,g34)
    c: InternalAlignment(g32,g34)
    c: InternalAlignment(g33,g34)
    c: InternalAlignment(g35,g34)
    c: InternalAlignment(g36,g34)
    c: Block(g34)
    c: Block(g28)
    c: Weight(g37) = 1
    c: Equal(g37,g38)
    c: Equal(g37,g39)
    c: InternalAlignment(g37,g40)
    c: InternalAlignment(g38,g40)
    c: InternalAlignment(g39,g40)
    c: InternalAlignment(g41,g40)
    c: InternalAlignment(g42,g40)
    c: Weight(g43) = 1
    c: Equal(g43,g44)
    c: Equal(g43,g45)
    c: InternalAlignment(g43,g46)
    c: InternalAlignment(g44,g46)
    c: InternalAlignment(g45,g46)
    c: InternalAlignment(g47,g46)
    c: InternalAlignment(g48,g46)
    c: Block(g40)
    c: Block(g46)
    c: Coincident(g49,g4)
    c: Coincident(g49,g3)
    c: Horizontal(g49)
    c: Distance(g49) = 450
    c: Coincident(g50,g4)
    c: Coincident(g50,g3)
    c: Horizontal(g50)
    c: Horizontal(g51)
    c: Coincident(g2,g51)
    c: Block(g51)
    c: Coincident(g1,g51)
    c: Weight(g52) = 1
    c: Equal(g52,g53)
    c: Equal(g52,g54)
    c: InternalAlignment(g52,g55)
    c: InternalAlignment(g53,g55)
    c: InternalAlignment(g54,g55)
    c: InternalAlignment(g56,g55)
    c: InternalAlignment(g57,g55)
    c: Block(g55)
    c: Weight(g58) = 1
    c: Equal(g58,g59)
    c: Equal(g58,g60)
    c: InternalAlignment(g58,g61)
    c: InternalAlignment(g59,g61)
    c: InternalAlignment(g60,g61)
    c: InternalAlignment(g62,g61)
    c: InternalAlignment(g63,g61)
    c: Block(g61)
    c: Weight(g64) = 1
    c: Equal(g64,g65)
    c: Equal(g64,g66)
    c: InternalAlignment(g64,g67)
    c: InternalAlignment(g65,g67)
    c: InternalAlignment(g66,g67)
    c: InternalAlignment(g68,g67)
    c: InternalAlignment(g69,g67)
    c: Block(g67)
    c: Weight(g70) = 1
    c: Equal(g70,g71)
    c: Equal(g70,g72)
    c: InternalAlignment(g70,g73)
    c: InternalAlignment(g71,g73)
    c: InternalAlignment(g72,g73)
    c: InternalAlignment(g74,g73)
    c: InternalAlignment(g75,g73)
    c: Block(g73)
    c: Weight(g76) = 1
    c: Equal(g76,g77)
    c: Equal(g76,g78)
    c: InternalAlignment(g76,g79)
    c: InternalAlignment(g77,g79)
    c: InternalAlignment(g78,g79)
    c: InternalAlignment(g80,g79)
    c: InternalAlignment(g81,g79)
    c: Weight(g82) = 1
    c: Equal(g82,g83)
    c: Equal(g82,g84)
    c: InternalAlignment(g82,g85)
    c: InternalAlignment(g83,g85)
    c: InternalAlignment(g84,g85)
    c: InternalAlignment(g86,g85)
    c: InternalAlignment(g87,g85)
    c: Block(g79)
    c: Block(g85)
    c: Coincident(g88,g79)
    c: Coincident(g88,g85)
    c: Vertical(g88)
    c: Coincident(g89,g79)
    c: Coincident(g89,g61)
    c: Coincident(g90,g61)
    c: Coincident(g90,g85)
    c: Weight(g91) = 1
    c: Equal(g91,g92)
    c: Equal(g91,g93)
    c: InternalAlignment(g91,g94)
    c: InternalAlignment(g92,g94)
    c: InternalAlignment(g93,g94)
    c: InternalAlignment(g95,g94)
    c: InternalAlignment(g96,g94)
    c: Weight(g97) = 1
    c: Equal(g97,g98)
    c: Equal(g97,g99)
    c: InternalAlignment(g97,g100)
    c: InternalAlignment(g98,g100)
    c: InternalAlignment(g99,g100)
    c: InternalAlignment(g101,g100)
    c: InternalAlignment(g102,g100)
    c: Block(g94)
    c: Block(g100)
    c: Coincident(g103,g94)
    c: Coincident(g103,g100)
    c: Vertical(g103)
    c: Coincident(g104,g94)
    c: Coincident(g104,g55)
    c: Coincident(g105,g55)
    c: Coincident(g105,g100)
    c: Weight(g106) = 1
    c: Equal(g106,g107)
    c: Equal(g106,g108)
    c: InternalAlignment(g106,g109)
    c: InternalAlignment(g107,g109)
    c: InternalAlignment(g108,g109)
    c: InternalAlignment(g110,g109)
    c: InternalAlignment(g111,g109)
    c: Weight(g112) = 1
    c: Equal(g112,g113)
    c: Equal(g112,g114)
    c: InternalAlignment(g112,g115)
    c: InternalAlignment(g113,g115)
    c: InternalAlignment(g114,g115)
    c: InternalAlignment(g116,g115)
    c: InternalAlignment(g117,g115)
    c: Block(g109)
    c: Block(g115)
    c: Coincident(g118,g109)
    c: Coincident(g118,g115)
    c: Vertical(g118)
    c: Coincident(g119,g115)
    c: Coincident(g119,g73)
    c: Coincident(g120,g73)
    c: Coincident(g120,g109)
    c: Weight(g121) = 1
    c: Equal(g121,g122)
    c: Equal(g121,g123)
    c: InternalAlignment(g121,g124)
    c: InternalAlignment(g122,g124)
    c: InternalAlignment(g123,g124)
    c: InternalAlignment(g125,g124)
    c: InternalAlignment(g126,g124)
    c: Weight(g127) = 1
    c: Equal(g127,g128)
    c: Equal(g127,g129)
    c: InternalAlignment(g127,g130)
    c: InternalAlignment(g128,g130)
    c: InternalAlignment(g129,g130)
    c: InternalAlignment(g131,g130)
    c: InternalAlignment(g132,g130)
    c: Block(g124)
    c: Block(g130)
    c: Coincident(g133,g124)
    c: Coincident(g133,g130)
    c: Vertical(g133)
    c: Coincident(g134,g130)
    c: Coincident(g134,g67)
    c: Coincident(g135,g67)
    c: Coincident(g135,g124)
    c: Weight(g136) = 1
    c: Equal(g136,g137)
    c: Equal(g136,g138)
    c: InternalAlignment(g136,g139)
    c: InternalAlignment(g137,g139)
    c: InternalAlignment(g138,g139)
    c: InternalAlignment(g140,g139)
    c: InternalAlignment(g141,g139)
    c: Weight(g142) = 1
    c: Equal(g142,g143)
    c: Equal(g142,g144)
    c: InternalAlignment(g142,g145)
    c: InternalAlignment(g143,g145)
    c: InternalAlignment(g144,g145)
    c: InternalAlignment(g146,g145)
    c: InternalAlignment(g147,g145)
    c: Weight(g148) = 1
    c: Equal(g148,g149)
    c: Equal(g148,g150)
    c: InternalAlignment(g148,g151)
    c: InternalAlignment(g149,g151)
    c: InternalAlignment(g150,g151)
    c: InternalAlignment(g152,g151)
    c: InternalAlignment(g153,g151)
    c: Weight(g154) = 1
    c: Equal(g154,g155)
    c: Equal(g154,g156)
    c: InternalAlignment(g154,g157)
    c: InternalAlignment(g155,g157)
    c: InternalAlignment(g156,g157)
    c: InternalAlignment(g158,g157)
    c: InternalAlignment(g159,g157)
    c: Block(g157)
    c: Block(g151)
    c: Block(g145)
    c: Block(g139)
    c: Coincident(g160,g34)
    c: Coincident(g160,g157)
    c: Coincident(g161,g157)
    c: Coincident(g161,g151)
    c: Horizontal(g161)
    c: Coincident(g162,g151)
    c: Coincident(g162,g34)
    c: Vertical(g162)
    c: Coincident(g163,g28)
    c: Coincident(g163,g145)
    c: Vertical(g163)
    c: Coincident(g164,g145)
    c: Coincident(g164,g139)
    c: Horizontal(g164)
    c: Coincident(g165,g139)
    c: Coincident(g165,g28)
    c: Weight(g166) = 1
    c: Equal(g166,g167)
    c: Equal(g166,g168)
    c: InternalAlignment(g166,g169)
    c: InternalAlignment(g167,g169)
    c: InternalAlignment(g168,g169)
    c: InternalAlignment(g170,g169)
    c: InternalAlignment(g171,g169)
    c: Weight(g172) = 1
    c: Equal(g172,g173)
    c: Equal(g172,g174)
    c: InternalAlignment(g172,g175)
    c: InternalAlignment(g173,g175)
    c: InternalAlignment(g174,g175)
    c: InternalAlignment(g176,g175)
    c: InternalAlignment(g177,g175)
    c: Weight(g178) = 1
    c: Equal(g178,g179)
    c: Equal(g178,g180)
    c: InternalAlignment(g178,g181)
    c: InternalAlignment(g179,g181)
    c: InternalAlignment(g180,g181)
    c: InternalAlignment(g182,g181)
    c: InternalAlignment(g183,g181)
    c: Weight(g184) = 1
    c: Equal(g184,g185)
    c: Equal(g184,g186)
    c: InternalAlignment(g184,g187)
    c: InternalAlignment(g185,g187)
    c: InternalAlignment(g186,g187)
    c: InternalAlignment(g188,g187)
    c: InternalAlignment(g189,g187)
    c: Block(g187)
    c: Block(g181)
    c: Block(g175)
    c: Block(g169)
    c: Coincident(g190,g187)
    c: Coincident(g190,g181)
    c: Horizontal(g190)
    c: Coincident(g191,g181)
    c: Coincident(g191,g16)
    c: Vertical(g191)
    c: Coincident(g192,g22)
    c: Coincident(g192,g175)
    c: Vertical(g192)
    c: Coincident(g193,g175)
    c: Coincident(g193,g169)
    c: Horizontal(g193)
    c: Coincident(g194,g169)
    c: Coincident(g194,g22)
    c: Coincident(g195,g16)
    c: Weight(g196) = 1
    c: Equal(g196,g197)
    c: Equal(g196,g198)
    c: InternalAlignment(g196,g199)
    c: InternalAlignment(g197,g199)
    c: InternalAlignment(g198,g199)
    c: InternalAlignment(g200,g199)
    c: InternalAlignment(g201,g199)
    c: Weight(g202) = 1
    c: Equal(g202,g203)
    c: Equal(g202,g204)
    c: InternalAlignment(g202,g205)
    c: InternalAlignment(g203,g205)
    c: InternalAlignment(g204,g205)
    c: InternalAlignment(g206,g205)
    c: InternalAlignment(g207,g205)
    c: Block(g205)
    c: Block(g199)
    c: Coincident(g208,g205)
    c: Coincident(g208,g40)
    c: Coincident(g209,g40)
    c: Coincident(g209,g199)
    c: Coincident(g210,g199)
    c: Coincident(g210,g205)
    c: Vertical(g210)
    c: Weight(g211) = 1
    c: Equal(g211,g212)
    c: Equal(g211,g213)
    c: InternalAlignment(g211,g214)
    c: InternalAlignment(g212,g214)
    c: InternalAlignment(g213,g214)
    c: InternalAlignment(g215,g214)
    c: InternalAlignment(g216,g214)
    c: Weight(g217) = 1
    c: Equal(g217,g218)
    c: Equal(g217,g219)
    c: InternalAlignment(g217,g220)
    c: InternalAlignment(g218,g220)
    c: InternalAlignment(g219,g220)
    c: InternalAlignment(g221,g220)
    c: InternalAlignment(g222,g220)
    c: Block(g220)
    c: Block(g214)
    c: Coincident(g223,g214)
    c: Coincident(g223,g46)
    c: Coincident(g224,g46)
    c: Coincident(g224,g220)
    c: Coincident(g225,g220)
    c: Coincident(g225,g214)
    c: Vertical(g225)
    c: Horizontal(g226)
    c: Block(g226)
    c: Vertical(g227)
    c: Block(g227)
    c: Block(g228)
    c: Weight(g229) = 1
    c: Equal(g229,g230)
    c: Equal(g229,g231)
    c: InternalAlignment(g229,g232)
    c: InternalAlignment(g230,g232)
    c: InternalAlignment(g231,g232)
    c: InternalAlignment(g233,g232)
    c: InternalAlignment(g234,g232)
    c: Weight(g235) = 1
    c: Equal(g235,g236)
    c: Equal(g235,g237)
    c: InternalAlignment(g235,g238)
    c: InternalAlignment(g236,g238)
    c: InternalAlignment(g237,g238)
    c: InternalAlignment(g239,g238)
    c: InternalAlignment(g240,g238)
    c: Weight(g241) = 1
    c: Equal(g241,g242)
    c: Equal(g241,g243)
    c: InternalAlignment(g241,g244)
    c: InternalAlignment(g242,g244)
    c: InternalAlignment(g243,g244)
    c: InternalAlignment(g245,g244)
    c: InternalAlignment(g246,g244)
    c: Weight(g247) = 1
    c: Equal(g247,g248)
    c: Equal(g247,g249)
    c: InternalAlignment(g247,g250)
    c: InternalAlignment(g248,g250)
    c: InternalAlignment(g249,g250)
    c: InternalAlignment(g251,g250)
    c: InternalAlignment(g252,g250)
    c: Block(g232)
    c: Block(g238)
    c: Block(g244)
    c: Block(g250)
    c: Coincident(g253,g238)
    c: Coincident(g253,g232)
    c: Horizontal(g253)
    c: Block(g195)
    c: Weight(g254) = 1
    c: Equal(g254,g255)
    c: Equal(g254,g256)
    c: InternalAlignment(g254,g257)
    c: InternalAlignment(g255,g257)
    c: InternalAlignment(g256,g257)
    c: InternalAlignment(g258,g257)
    c: InternalAlignment(g259,g257)
    c: Weight(g260) = 1
    c: Equal(g260,g261)
    c: Equal(g260,g262)
    c: InternalAlignment(g260,g263)
    c: InternalAlignment(g261,g263)
    c: InternalAlignment(g262,g263)
    c: InternalAlignment(g264,g263)
    c: InternalAlignment(g265,g263)
    c: Weight(g266) = 1
    c: Equal(g266,g267)
    c: Equal(g266,g268)
    c: InternalAlignment(g266,g269)
    c: InternalAlignment(g267,g269)
    c: InternalAlignment(g268,g269)
    c: InternalAlignment(g270,g269)
    c: InternalAlignment(g271,g269)
    c: Block(g257)
    c: Block(g263)
    c: Block(g269)
    c: Coincident(g272,g269)
    c: Coincident(g345,g257)
    c: Vertical(g272)
    c: Coincident(g273,g257)
    c: Coincident(g273,g263)
    c: Coincident(g274,g263)
    c: Vertical(g274)
    c: Weight(g275) = 1
    c: Equal(g275,g276)
    c: Equal(g275,g277)
    c: InternalAlignment(g275,g278)
    c: InternalAlignment(g276,g278)
    c: InternalAlignment(g277,g278)
    c: InternalAlignment(g279,g278)
    c: InternalAlignment(g280,g278)
    c: Weight(g281) = 1
    c: Equal(g281,g282)
    c: Equal(g281,g283)
    c: InternalAlignment(g281,g284)
    c: InternalAlignment(g282,g284)
    c: InternalAlignment(g283,g284)
    c: InternalAlignment(g285,g284)
    c: InternalAlignment(g286,g284)
    c: Weight(g287) = 1
    c: Equal(g287,g288)
    c: Equal(g287,g289)
    c: InternalAlignment(g287,g290)
    c: InternalAlignment(g288,g290)
    c: InternalAlignment(g289,g290)
    c: InternalAlignment(g291,g290)
    c: InternalAlignment(g292,g290)
    c: Block(g290)
    c: Block(g284)
    c: Block(g278)
    c: Coincident(g293,g284)
    c: Coincident(g293,g278)
    c: Coincident(g294,g278)
    c: Coincident(g294,g290)
    c: Vertical(g294)
    c: Coincident(g295,g290)
    c: Coincident(g295,g284)
    c: Horizontal(g295)
    c: Weight(g296) = 1
    c: Equal(g296,g297)
    c: InternalAlignment(g296,g298)
    c: InternalAlignment(g297,g298)
    c: InternalAlignment(g299,g298)
    c: InternalAlignment(g300,g298)
    c: Weight(g301) = 1
    c: Equal(g301,g302)
    c: Equal(g301,g303)
    c: InternalAlignment(g301,g304)
    c: InternalAlignment(g302,g304)
    c: InternalAlignment(g303,g304)
    c: InternalAlignment(g305,g304)
    c: InternalAlignment(g306,g304)
    c: Weight(g307) = 1
    c: Equal(g307,g308)
    c: Equal(g307,g309)
    c: InternalAlignment(g307,g310)
    c: InternalAlignment(g308,g310)
    c: InternalAlignment(g309,g310)
    c: InternalAlignment(g311,g310)
    c: InternalAlignment(g312,g310)
    c: Equal(g313,g314)
    c: Equal(g313,g315)
    c: InternalAlignment(g313,g316)
    c: InternalAlignment(g314,g316)
    c: InternalAlignment(g315,g316)
    c: InternalAlignment(g317,g316)
    c: InternalAlignment(g318,g316)
    c: Block(g304)
    c: Block(g310)
    c: Block(g316)
    c: Block(g298)
    c: Coincident(g319,g298)
    c: Coincident(g319,g304)
    c: Horizontal(g319)
    c: Coincident(g320,g304)
    c: Coincident(g320,g310)
    c: Vertical(g320)
    c: Coincident(g321,g310)
    c: Coincident(g321,g316)
    c: Horizontal(g321)
    c: Coincident(g322,g316)
    c: Coincident(g322,g298)
    c: Weight(g323) = 1
    c: Equal(g323,g324)
    c: Equal(g323,g325)
    c: InternalAlignment(g323,g326)
    c: InternalAlignment(g324,g326)
    c: InternalAlignment(g325,g326)
    c: InternalAlignment(g327,g326)
    c: InternalAlignment(g328,g326)
    c: Weight(g329) = 1
    c: Equal(g329,g330)
    c: Equal(g329,g331)
    c: InternalAlignment(g329,g332)
    c: InternalAlignment(g330,g332)
    c: InternalAlignment(g331,g332)
    c: InternalAlignment(g333,g332)
    c: InternalAlignment(g334,g332)
    c: Weight(g335) = 1
    c: Equal(g335,g336)
    c: Equal(g335,g337)
    c: InternalAlignment(g335,g338)
    c: InternalAlignment(g336,g338)
    c: InternalAlignment(g337,g338)
    c: InternalAlignment(g339,g338)
    c: InternalAlignment(g340,g338)
    c: Block(g338)
    c: Block(g332)
    c: Block(g326)
    c: Coincident(g341,g338)
    c: Coincident(g341,g332)
    c: Horizontal(g341)
    c: Coincident(g342,g332)
    c: Coincident(g342,g326)
    c: Vertical(g342)
    c: Coincident(g343,g326)
    c: Coincident(g343,g338)
    c: Block(g344)
    c: PointOnObject(g272,g266)
    c: Coincident(g345,g344)
    c: Tangent(g272,g345)
    c: Coincident(g274,g344)
    c: Horizontal(g346)
    c: Distance(g346) = 4
    c: Coincident(g346,g274)
    c: InternalAlignment(g347,g348)
    c: InternalAlignment(g349,g348)
    c: InternalAlignment(g350,g348)
    c: Block(g348)
    c: Coincident(g350,g346)
FEATURE [Sketcher::SketchObject] Sketch001
  FullyConstrained = true
  MapMode = 4
  Placement = pos=(0,0,0) rot=(0.57735,0.57735,0.57735;2.0944rad)
  Support = -> [Sketch]
  sketch-geometry (46):
    g0: BSplineCurve PolesCount=3 KnotsCount=2 Degree=2 IsPeriodic=0
    g1: ArcOfCircle CenterX=73.1223 CenterY=-32.291 CenterZ=0 NormalX=0 NormalY=0 NormalZ=1 AngleXU=0 Radius=13 StartAngle=5.92268 EndAngle=9.06428
    g2: ArcOfCircle CenterX=66.7816 CenterY=-49.1439 CenterZ=0 NormalX=0 NormalY=0 NormalZ=1 AngleXU=0 Radius=13 StartAngle=2.78068 EndAngle=5.92131
    g3: ArcOfCircle CenterX=55.9263 CenterY=-78.1807 CenterZ=0 NormalX=0 NormalY=0 NormalZ=1 AngleXU=0 Radius=13 StartAngle=5.92268 EndAngle=9.06428
    g4: ArcOfCircle CenterX=49.5884 CenterY=-95.0342 CenterZ=0 NormalX=0 NormalY=0 NormalZ=1 AngleXU=0 Radius=13 StartAngle=2.78068 EndAngle=5.92131
    g5: ArcOfCircle CenterX=38.7206 CenterY=-124.067 CenterZ=0 NormalX=0 NormalY=0 NormalZ=1 AngleXU=0 Radius=13 StartAngle=5.92268 EndAngle=9.06428
    g6: ArcOfCircle CenterX=32.3875 CenterY=-140.92 CenterZ=0 NormalX=0 NormalY=0 NormalZ=1 AngleXU=0 Radius=13 StartAngle=2.78068 EndAngle=5.92131
    g7: ArcOfCircle CenterX=21.4715 CenterY=-169.934 CenterZ=0 NormalX=0 NormalY=0 NormalZ=1 AngleXU=0 Radius=13 StartAngle=5.92268 EndAngle=9.06428
    g8: ArcOfCircle CenterX=15.1336 CenterY=-186.787 CenterZ=0 NormalX=0 NormalY=0 NormalZ=1 AngleXU=0 Radius=13 StartAngle=2.78068 EndAngle=5.92131
    g9-g12: Circle x4 (B-spline internal-alignment scaffolding for g13; pole/knot coordinates omitted)
    g13: BSplineCurve PolesCount=4 KnotsCount=2 Degree=3 IsPeriodic=0
    g14: GeomPoint X=28.8094 Y=-19.0875 Z=0
    g15: GeomPoint X=47.0443 Y=-50.4712 Z=0
    g16: Circle CenterX=53.5586 CenterY=-23.2695 CenterZ=0 NormalX=0 NormalY=0 NormalZ=1 AngleXU=0 Radius=3.24518
    g17: Circle CenterX=-195.441 CenterY=-127.082 CenterZ=0 NormalX=0 NormalY=0 NormalZ=1 AngleXU=0 Radius=1
    g18: Circle CenterX=-8.24091 CenterY=-197.481 CenterZ=0 NormalX=0 NormalY=0 NormalZ=1 AngleXU=0 Radius=1
    g19: Circle CenterX=12.8789 CenterY=-141.321 CenterZ=0 NormalX=0 NormalY=0 NormalZ=1 AngleXU=0 Radius=1
    g20: BSplineCurve PolesCount=3 KnotsCount=2 Degree=2 IsPeriodic=0
    g21: GeomPoint X=-195.441 Y=-127.082 Z=0
    g22: GeomPoint X=12.8789 Y=-141.321 Z=0
    g23: Circle CenterX=-12.8016 CenterY=-179.036 CenterZ=0 NormalX=0 NormalY=0 NormalZ=1 AngleXU=0 Radius=10.5072
    g24: Circle CenterX=0.933922 CenterY=-166.43 CenterZ=0 NormalX=0 NormalY=0 NormalZ=1 AngleXU=0 Radius=3.26661
    g25: Circle CenterX=-33.5518 CenterY=-176.44 CenterZ=0 NormalX=0 NormalY=0 NormalZ=1 AngleXU=0 Radius=5.64388
    g26: Circle CenterX=-47.2366 CenterY=-173.859 CenterZ=0 NormalX=0 NormalY=0 NormalZ=1 AngleXU=0 Radius=3.01653
    g27: Circle CenterX=-56.2595 CenterY=-171.456 CenterZ=0 NormalX=0 NormalY=0 NormalZ=1 AngleXU=0 Radius=2.12826
    g28: ArcOfCircle CenterX=51.2151 CenterY=-198.473 CenterZ=0 NormalX=0 NormalY=0 NormalZ=1 AngleXU=0 Radius=20 StartAngle=2.78189 EndAngle=4.35269
    g29: LineSegment StartX=32.4951 StartY=-191.433 StartZ=0 EndX=94.6578 EndY=-26.1352 EndZ=0
    g30: LineSegment StartX=43.1192 StartY=-220.001 StartZ=0 EndX=-196.497 EndY=-129.89 EndZ=0
    g31: LineSegment StartX=43.1192 StartY=-220.001 StartZ=0 EndX=44.1752 EndY=-217.193 EndZ=0
    g32: LineSegment StartX=117.223 StartY=-19.0875 StartZ=0 EndX=117.223 EndY=-16.0875 EndZ=0
    g33: LineSegment StartX=117.223 StartY=-16.0875 StartZ=0 EndX=17.2232 EndY=-16.0875 EndZ=0
    g34: LineSegment StartX=17.2232 StartY=-16.0875 StartZ=0 EndX=17.2232 EndY=-19.0875 EndZ=0
    g35: LineSegment StartX=28.8094 StartY=-19.0875 StartZ=0 EndX=17.2232 EndY=-19.0875 EndZ=0
    g36: LineSegment StartX=47.0443 StartY=-50.4712 StartZ=0 EndX=12.8789 EndY=-141.321 EndZ=0
    g37: LineSegment StartX=-195.441 StartY=-127.082 StartZ=0 EndX=-196.497 EndY=-129.89 EndZ=0
    g38: LineSegment StartX=85.2866 StartY=-36.8766 StartZ=0 EndX=78.9396 EndY=-53.7463 EndZ=0
    g39: LineSegment StartX=60.9579 StartY=-27.7053 StartZ=0 EndX=54.6191 EndY=-44.5532 EndZ=0
    g40: LineSegment StartX=68.0907 StartY=-82.7664 StartZ=0 EndX=61.7465 EndY=-99.6365 EndZ=0
    g41: LineSegment StartX=43.7619 StartY=-73.595 StartZ=0 EndX=37.426 EndY=-90.4435 EndZ=0
    g42: LineSegment StartX=50.885 StartY=-128.652 StartZ=0 EndX=44.5456 EndY=-145.522 EndZ=0
    g43: LineSegment StartX=26.5562 StartY=-119.481 StartZ=0 EndX=20.2251 EndY=-136.329 EndZ=0
    g44: LineSegment StartX=9.3071 StartY=-165.349 StartZ=0 EndX=2.97115 EndY=-182.197 EndZ=0
    g45: LineSegment StartX=33.6358 StartY=-174.52 StartZ=0 EndX=27.2917 EndY=-191.39 EndZ=0
  constraints (71):
    c: Block(g0)
    c: Block(g1)
    c: Block(g2)
    c: Block(g4)
    c: Block(g3)
    c: Block(g6)
    c: Block(g5)
    c: Block(g8)
    c: Block(g7)
    c: Weight(g9) = 1
    c: Equal(g9,g10)
    c: Equal(g9,g11)
    c: Equal(g9,g12)
    c: InternalAlignment(g9-g12 -> g13) x4
    c: InternalAlignment(g14,g13)
    c: InternalAlignment(g15,g13)
    c: Block(g16)
    c: Weight(g17) = 1
    c: Equal(g17,g18)
    c: Equal(g17,g19)
    c: InternalAlignment(g17,g20)
    c: InternalAlignment(g18,g20)
    c: InternalAlignment(g19,g20)
    c: InternalAlignment(g21,g20)
    c: InternalAlignment(g22,g20)
    c: Block(g20)
    c: Block(g23)
    c: Block(g24)
    c: Block(g25)
    c: Block(g26)
    c: Block(g27)
    c: Block(g28)
    c: Coincident(g29,g28)
    c: Coincident(g29,g0)
    c: Block(g13)
    c: Coincident(g31,g30)
    c: Coincident(g31,g28)
    c: Block(g31)
    c: Coincident(g32,g0)
    c: Vertical(g32)
    c: Coincident(g33,g32)
    c: Horizontal(g33)
    c: Coincident(g34,g33)
    c: Vertical(g34)
    c: Block(g33)
    c: Coincident(g35,g13)
    c: Coincident(g35,g34)
    c: Horizontal(g35)
    c: Coincident(g36,g13)
    c: Coincident(g36,g20)
    c: Coincident(g37,g20)
    c: Coincident(g37,g30)
    c: Block(g30)
    c: Coincident(g38,g1)
    c: Coincident(g38,g2)
    c: Coincident(g39,g1)
    c: Coincident(g39,g2)
    c: Coincident(g40,g3)
    c: Coincident(g40,g4)
    c: Coincident(g41,g3)
    c: Coincident(g41,g4)
    c: Coincident(g42,g5)
    c: Coincident(g42,g6)
    c: Coincident(g43,g5)
    c: Coincident(g43,g6)
    c: Coincident(g44,g7)
    c: Coincident(g44,g8)
    c: Coincident(g45,g7)
    c: Coincident(g45,g8)
    c: Distance(g30) = 256
    c: Distance(g33) = 100
FEATURE [Part::Extrusion] Extrude002
  Base = -> Sketch001
  Dir = (1,0,0)
  DirMode = 2
  FaceMakerClass = Part::FaceMakerBullseye
  LengthFwd = 8
  LengthRev = 0
  Solid = true
  Symmetric = false
FEATURE [Sketcher::SketchObject] Sketch002
  FullyConstrained = true
  sketch-geometry (20):
    g0: LineSegment StartX=-2.77179 StartY=-200.304 StartZ=0 EndX=5.22821 EndY=-200.304 EndZ=0
    g1: LineSegment StartX=5.22821 StartY=-200.304 StartZ=0 EndX=5.22821 EndY=-197.304 EndZ=0
    g2: LineSegment StartX=-2.77179 StartY=-200.304 StartZ=0 EndX=-2.77179 EndY=-197.304 EndZ=0
    g3: LineSegment StartX=5.22821 StartY=-197.304 StartZ=0 EndX=8.22821 EndY=-197.304 EndZ=0
    g4: LineSegment StartX=-2.77179 StartY=-197.304 StartZ=0 EndX=-5.77179 EndY=-197.304 EndZ=0
    g5: LineSegment StartX=19.2282 StartY=-203.304 StartZ=0 EndX=19.2282 EndY=-206.304 EndZ=0
    g6: LineSegment StartX=-16.7718 StartY=-203.304 StartZ=0 EndX=-16.7718 EndY=-206.304 EndZ=0
    g7: LineSegment StartX=-16.7718 StartY=-206.304 StartZ=0 EndX=19.2282 EndY=-206.304 EndZ=0
    g8: Circle CenterX=-16.7718 CenterY=-203.304 CenterZ=0 NormalX=0 NormalY=0 NormalZ=1 AngleXU=0 Radius=1
    g9: Circle CenterX=-5.77179 CenterY=-203.304 CenterZ=0 NormalX=0 NormalY=0 NormalZ=1 AngleXU=0 Radius=1
    g10: Circle CenterX=-5.77179 CenterY=-197.304 CenterZ=0 NormalX=0 NormalY=0 NormalZ=1 AngleXU=0 Radius=1
    g11: BSplineCurve PolesCount=3 KnotsCount=2 Degree=2 IsPeriodic=0
    g12: GeomPoint X=-16.7718 Y=-203.304 Z=0
    g13: GeomPoint X=-5.77179 Y=-197.304 Z=0
    g14: Circle CenterX=19.2282 CenterY=-203.304 CenterZ=0 NormalX=0 NormalY=0 NormalZ=1 AngleXU=0 Radius=1
    g15: Circle CenterX=8.22821 CenterY=-203.304 CenterZ=0 NormalX=0 NormalY=0 NormalZ=1 AngleXU=0 Radius=1
    g16: Circle CenterX=8.22821 CenterY=-197.304 CenterZ=0 NormalX=0 NormalY=0 NormalZ=1 AngleXU=0 Radius=1
    g17: BSplineCurve PolesCount=3 KnotsCount=2 Degree=2 IsPeriodic=0
    g18: GeomPoint X=19.2282 Y=-203.304 Z=0
    g19: GeomPoint X=8.22821 Y=-197.304 Z=0
  constraints (41):
    c: Horizontal(g0)
    c: Distance(g0) = 8
    c: Coincident(g1,g0)
    c: Vertical(g1)
    c: Distance(g1) = 3
    c: Coincident(g2,g0)
    c: Vertical(g2)
    c: Distance(g2) = 3
    c: Coincident(g3,g1)
    c: Horizontal(g3)
    c: Distance(g3) = 3
    c: Coincident(g4,g2)
    c: Horizontal(g4)
    c: Distance(g4) = 3
    c: Vertical(g5)
    c: Vertical(g6)
    c: Coincident(g7,g6)
    c: Coincident(g7,g5)
    c: Weight(g8) = 1
    c: Equal(g8,g9)
    c: Equal(g8,g10)
    c: Coincident(g11,g4)
    c: InternalAlignment(g8,g11)
    c: InternalAlignment(g9,g11)
    c: InternalAlignment(g10,g11)
    c: InternalAlignment(g12,g11)
    c: InternalAlignment(g13,g11)
    c: Coincident(g17,g5)
    c: Weight(g14) = 1
    c: Equal(g14,g15)
    c: Equal(g14,g16)
    c: Coincident(g17,g3)
    c: InternalAlignment(g14,g17)
    c: InternalAlignment(g15,g17)
    c: InternalAlignment(g16,g17)
    c: InternalAlignment(g18,g17)
    c: InternalAlignment(g19,g17)
    c: Block(g7)
    c: Block(g17)
    c: Block(g11)
    c: Block(g6)
FEATURE [Part::Extrusion] Extrude003
  Base = -> Sketch002
  Dir = (0,0,1)
  DirMode = 2
  FaceMakerClass = Part::FaceMakerBullseye
  LengthFwd = 260
  LengthRev = 0
  Solid = true
  Symmetric = false
FEATURE [Part::Extrusion] Extrude
  Base = -> Sketch
  Dir = (0,0,1)
  DirMode = 2
  FaceMakerClass = Part::FaceMakerBullseye
  LengthFwd = 14
  LengthRev = 0
  Solid = true
  Symmetric = false
